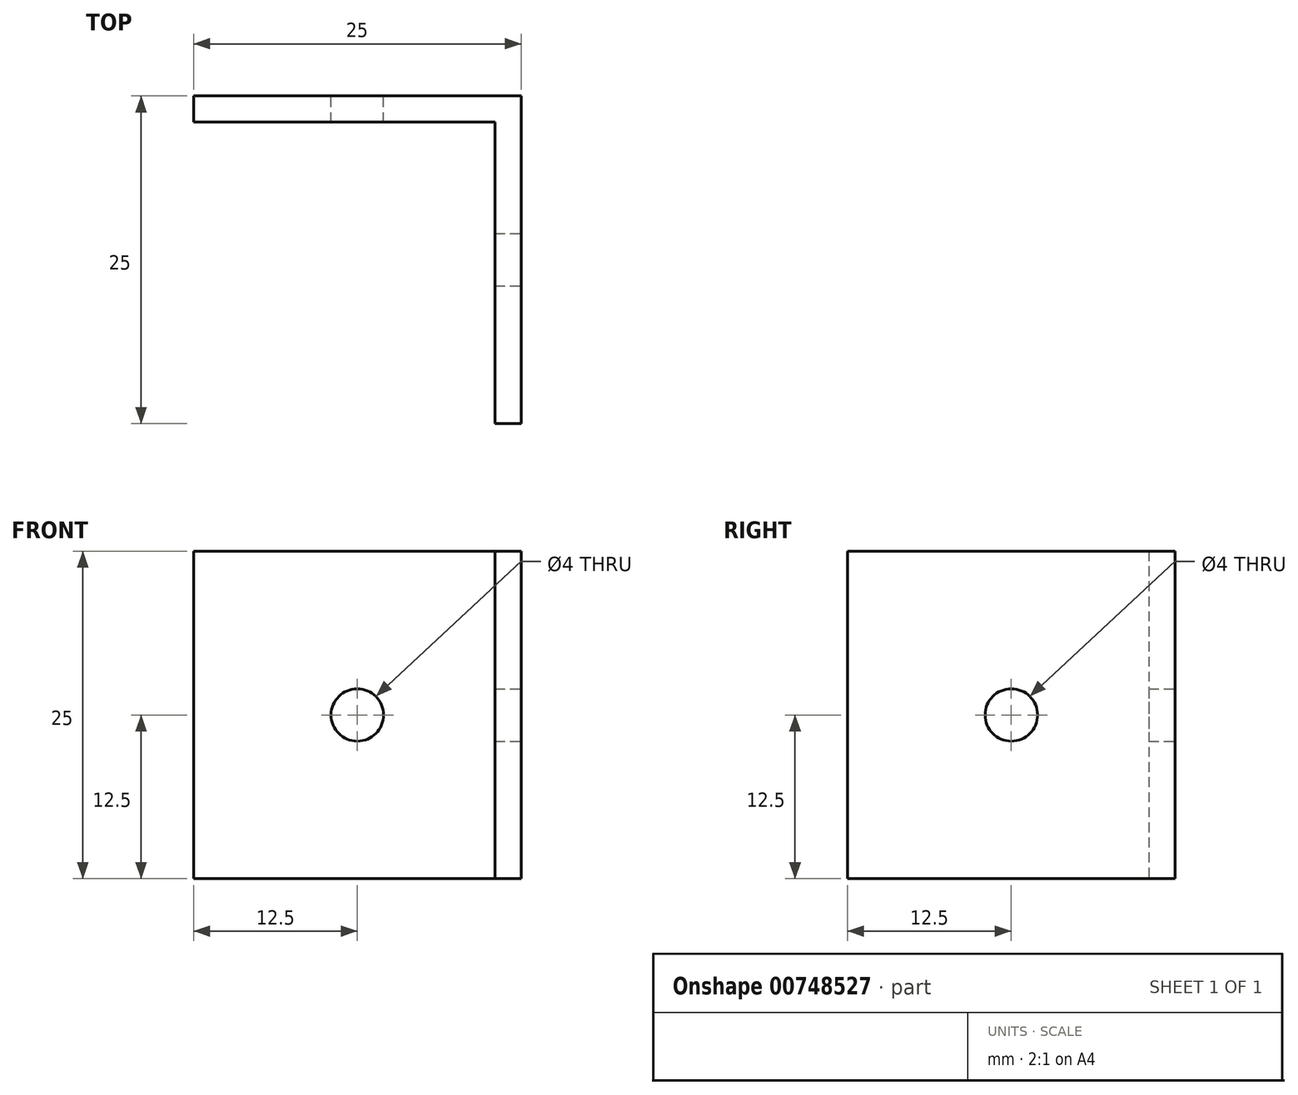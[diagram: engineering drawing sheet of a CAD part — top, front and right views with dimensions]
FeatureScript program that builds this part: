
annotation { "Feature Type Name" : "Feature", "Feature Type Description" : "" }
export const myFeature = defineFeature(function(context is Context, id is Id, definition is map)
    precondition{}
    {
        {
            var Q0;
            Q0=qCreatedBy(makeId("Top.planeOp"),FACE);
            var sketch = newSketch(context, id + "F0", { "sketchPlane" : qUnion([Q0])});
            skLineSegment(sketch, "E0.bottom", {"start": v(0, 0) * mm, "end": v(25, 0) * mm});
            skLineSegment(sketch, "E0.top", {"start": v(0, 25) * mm, "end": v(25, 25) * mm});
            skLineSegment(sketch, "E0.left", {"start": v(0, 0) * mm, "end": v(0, 25) * mm});
            skLineSegment(sketch, "E0.right", {"start": v(25, 0) * mm, "end": v(25, 25) * mm});
            skLineSegment(sketch, "E1.bottom", {"start": v(0, 0) * mm, "end": v(23, 0) * mm});
            skLineSegment(sketch, "E1.top", {"start": v(0, 23) * mm, "end": v(23, 23) * mm});
            skLineSegment(sketch, "E1.left", {"start": v(0, 0) * mm, "end": v(0, 23) * mm});
            skLineSegment(sketch, "E1.right", {"start": v(23, 0) * mm, "end": v(23, 23) * mm});
            skSolve(sketch);
        }
        {
            var Q0;
            {var subQ2=sQuery(id+"F0.wireOp",EDGE,"E0.top");Q0=makeQuery(id+"F0.imprint","IMPRINT",FACE,{"disambiguationData":[TD([[makeQuery(id+"F0.imprint","IMPRINT",EDGE,{"derivedFrom":subQ2}),-1.0]])]});}
            extrude(context, id + "F1", {"entities" : qUnion([Q0]), "depth" : 25 * mm, "offsetDistance" : 25 * mm});
        }
        {
            var Q0;
            Q0=makeQuery(id+"F1.opExtrude","SWEPT_FACE",FACE,{"disambiguationData":[OSD([sQuery(id+"F0.wireOp",EDGE,"E0.top")])]});
            var sketch = newSketch(context, id + "F2", { "sketchPlane" : qUnion([Q0])});
            skCircle(sketch, "E2", {"center": v(-12.5, 12.5) * mm, "radius": 2 * mm});
            skPoint(sketch, "E2.centerSnap0", {"position": v(0, 12.5) * mm});
            skPoint(sketch, "E2.centerSnap1", {"position": v(-12.5, 0) * mm});
            skSolve(sketch);
        }
        {
            var Q0;
            Q0 = qSketchRegion(id + "F2", true);
            extrude(context, id + "F3", {"entities" : qUnion([Q0]), "operationType" : NewBodyOperationType.REMOVE, "endBound" : BoundingType.THROUGH_ALL, "oppositeDirection" : true, "depth" : 25 * mm, "offsetDistance" : 25 * mm});
        }
        {
            var Q0;
            Q0=makeQuery(id+"F1.opExtrude","SWEPT_FACE",FACE,{"disambiguationData":[OSD([sQuery(id+"F0.wireOp",EDGE,"E0.right")])]});
            var sketch = newSketch(context, id + "F4", { "sketchPlane" : qUnion([Q0])});
            skCircle(sketch, "E3", {"center": v(12.5, 12.5) * mm, "radius": 2 * mm});
            skPoint(sketch, "E3.centerSnap0", {"position": v(25, 12.5) * mm});
            skPoint(sketch, "E3.centerSnap1", {"position": v(12.5, 0) * mm});
            skSolve(sketch);
        }
        {
            var Q0;
            Q0 = qSketchRegion(id + "F4", true);
            extrude(context, id + "F5", {"entities" : qUnion([Q0]), "operationType" : NewBodyOperationType.REMOVE, "endBound" : BoundingType.THROUGH_ALL, "oppositeDirection" : true, "depth" : 25 * mm, "offsetDistance" : 25 * mm});
        }
    });
